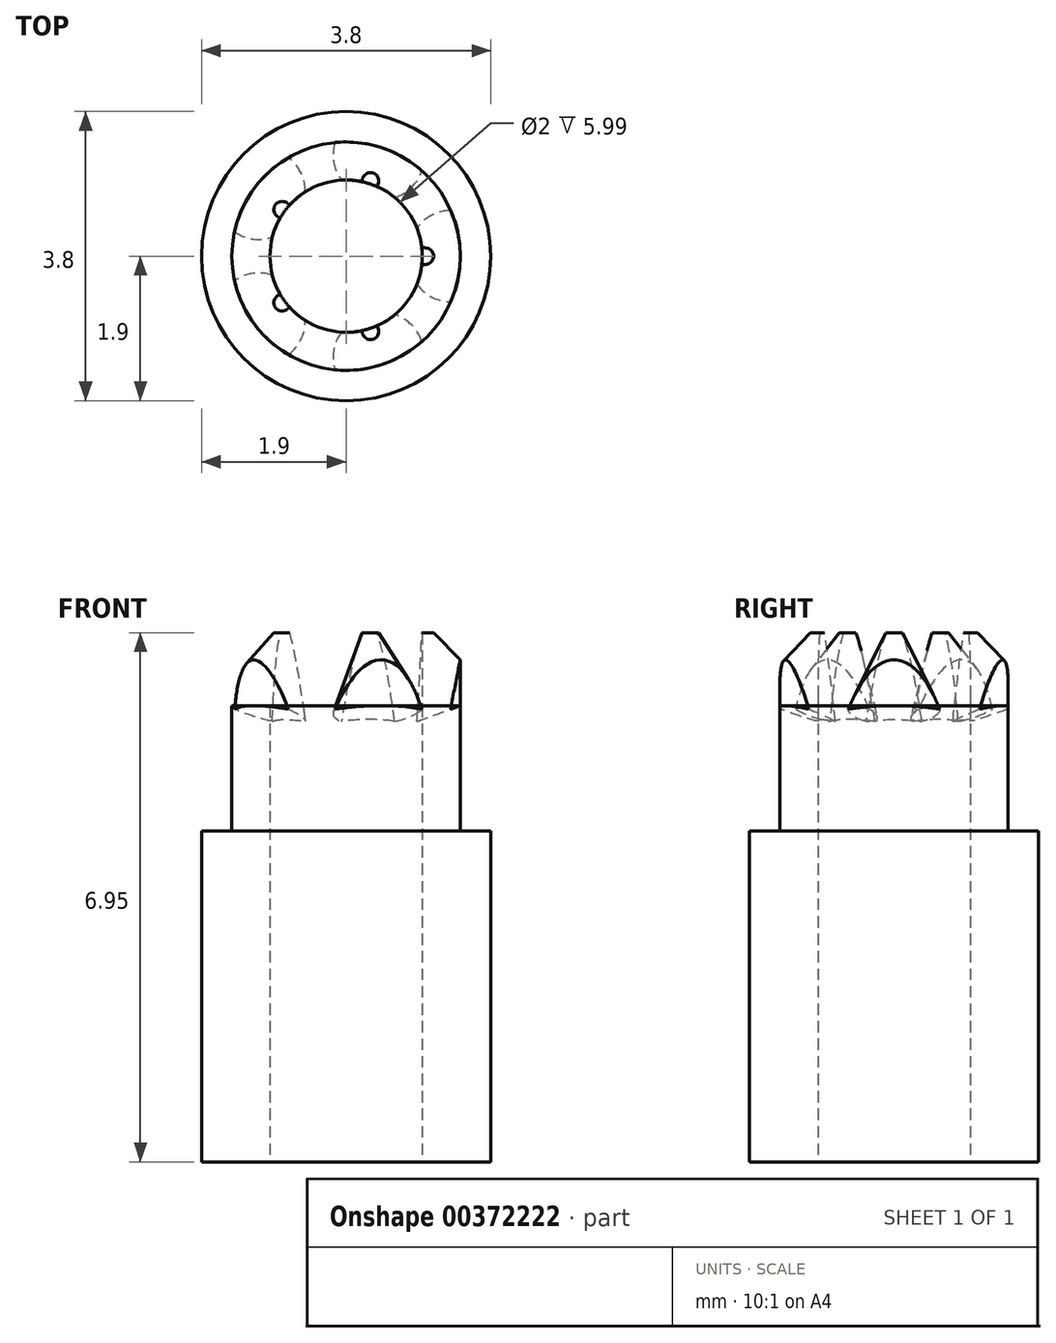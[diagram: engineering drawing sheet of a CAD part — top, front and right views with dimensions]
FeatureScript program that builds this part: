
annotation { "Feature Type Name" : "Feature", "Feature Type Description" : "" }
export const myFeature = defineFeature(function(context is Context, id is Id, definition is map)
    precondition{}
    {
        {
            var Q0;
            Q0=qCreatedBy(makeId("Top.planeOp"),FACE);
            var sketch = newSketch(context, id + "F0", { "sketchPlane" : qUnion([Q0])});
            skCircle(sketch, "E0", {"center": v(0, 0) * mm, "radius": 1 * mm});
            skCircle(sketch, "E1", {"center": v(0, 0) * mm, "radius": 1.5 * mm});
            skCircle(sketch, "E2", {"center": v(0, 0) * mm, "radius": 1.9 * mm});
            skSolve(sketch);
        }
        {
            var Q0;
            Q0=makeQuery(id+"F0.imprint","IMPRINT",FACE,{"disambiguationData":[TD([[makeQuery(id+"F0.imprint","IMPRINT",EDGE,{"derivedFrom":sQuery(id+"F0.wireOp",EDGE,"E0")}),-1.0]])]});
            extrude(context, id + "F1", {"entities" : qUnion([Q0]), "depth" : 2.6 * mm});
        }
        {
            var Q0;
            Q0=qCreatedBy(makeId("Top.planeOp"),FACE);
            cPlane(context, id + "F2", {"entities" : qUnion([Q0]), "cplaneType" : CPlaneType.OFFSET, "offset" : 1.6 * mm, "width" : 150 * mm, "height" : 150 * mm});
        }
        {
            var Q0;
            Q0=qCreatedBy(makeId("Front.planeOp"),FACE);
            var sketch = newSketch(context, id + "F3", { "sketchPlane" : qUnion([Q0])});
            skLineSegment(sketch, "E3", {"start": v(0, 0) * mm, "end": v(0, 1.6) * mm, "construction": true});
            skLineSegment(sketch, "E4", {"start": v(0, 1.6) * mm, "end": v(1.38, 1.6) * mm, "construction": true});
            skLineSegment(sketch, "E5", {"start": v(1.37, 1.6) * mm, "end": v(1.94, 1.8) * mm});
            skLineSegment(sketch, "E6", {"start": v(1.38, 1.6) * mm, "end": v(0.93, 2.82) * mm});
            skLineSegment(sketch, "E7", {"start": v(1.94, 1.8) * mm, "end": v(0.93, 2.82) * mm});
            skSolve(sketch);
        }
        {
            var Q0;
            Q0=makeQuery(id+"F3.imprint","IMPRINT",FACE,{"disambiguationData":[TD([[makeQuery(id+"F3.imprint","IMPRINT",EDGE,{"derivedFrom":sQuery(id+"F3.wireOp",EDGE,"E5")}),1.0]])]});
            var Q1;
            Q1=sQuery(id+"F3.wireOp",EDGE,"E6");
            revolve(context, id + "F4", {"entities" : qUnion([Q0]), "axis" : qUnion([Q1]), "revolveType" : RevolveType.FULL, "oppositeDirection" : true});
        }
        {
            var Q0;
            Q0=makeQuery(id+"F4.opRevolve","SWEPT_BODY",BODY,{"disambiguationData":[OSD([sQuery(id+"F3.wireOp",EDGE,"E5"),sQuery(id+"F3.wireOp",EDGE,"E6"),sQuery(id+"F3.wireOp",EDGE,"E7")])]});
            var Q1;
            Q1=sQuery(id+"F3.wireOp",EDGE,"E3");
            circularPattern(context, id + "F5", {"entities" : qUnion([Q0]), "axis" : qUnion([Q1]), "angle" : 72 * degree, "instanceCount" : round(5), "computeTransformsWithoutBuiltin" : true});
        }
        {
            var Q0;
            Q0=makeQuery(id+"F1.opExtrude","SWEPT_BODY",BODY,{"disambiguationData":[OSD([sQuery(id+"F0.wireOp",EDGE,"E0"),sQuery(id+"F0.wireOp",EDGE,"E1")])]});
            transform(context, id + "F6", {"entities" : qUnion([Q0]), "transformType" : TransformType.TRANSLATION_3D, "dx" : 0 * mm, "dy" : 0 * mm, "dz" : 0 * mm, "makeCopy" : true});
        }
        {
            var Q0;
            Q0=makeQuery(id+"F1.opExtrude","SWEPT_BODY",BODY,{"disambiguationData":[OSD([sQuery(id+"F0.wireOp",EDGE,"E0"),sQuery(id+"F0.wireOp",EDGE,"E1")])]});
            var Q1;
            Q1=makeQuery(id+"F4.opRevolve","SWEPT_BODY",BODY,{"disambiguationData":[OSD([sQuery(id+"F3.wireOp",EDGE,"E5"),sQuery(id+"F3.wireOp",EDGE,"E6"),sQuery(id+"F3.wireOp",EDGE,"E7")])]});
            booleanBodies(context, id + "F7", {"operationType" : BooleanOperationType.INTERSECTION, "tools" : qUnion([Q0, Q1])});
        }
        {
            var Q0;
            Q0=makeQuery(id+"F6.opPattern","COPY",BODY,{"derivedFrom":makeQuery(id+"F1.opExtrude","SWEPT_BODY",BODY,{"disambiguationData":[OSD([sQuery(id+"F0.wireOp",EDGE,"E0"),sQuery(id+"F0.wireOp",EDGE,"E1")])]}),"instanceName":"1"});
            transform(context, id + "F8", {"entities" : qUnion([Q0]), "transformType" : TransformType.TRANSLATION_3D, "dx" : 0 * mm, "dy" : 0 * mm, "dz" : 0 * mm, "makeCopy" : true});
        }
        {
            var Q0;
            Q0=makeQuery(id+"F8.opPattern","COPY",BODY,{"derivedFrom":makeQuery(id+"F6.opPattern","COPY",BODY,{"derivedFrom":makeQuery(id+"F1.opExtrude","SWEPT_BODY",BODY,{"disambiguationData":[OSD([sQuery(id+"F0.wireOp",EDGE,"E0"),sQuery(id+"F0.wireOp",EDGE,"E1")])]}),"instanceName":"1"}),"instanceName":"1"});
            transform(context, id + "F9", {"entities" : qUnion([Q0]), "transformType" : TransformType.TRANSLATION_3D, "dx" : 0 * mm, "dy" : 0 * mm, "dz" : 0 * mm, "makeCopy" : true});
        }
        {
            var Q0;
            Q0=makeQuery(id+"F9.opPattern","COPY",BODY,{"derivedFrom":makeQuery(id+"F8.opPattern","COPY",BODY,{"derivedFrom":makeQuery(id+"F6.opPattern","COPY",BODY,{"derivedFrom":makeQuery(id+"F1.opExtrude","SWEPT_BODY",BODY,{"disambiguationData":[OSD([sQuery(id+"F0.wireOp",EDGE,"E0"),sQuery(id+"F0.wireOp",EDGE,"E1")])]}),"instanceName":"1"}),"instanceName":"1"}),"instanceName":"1"});
            transform(context, id + "F10", {"entities" : qUnion([Q0]), "transformType" : TransformType.TRANSLATION_3D, "dx" : 0 * mm, "dy" : 0 * mm, "dz" : 0 * mm, "makeCopy" : true});
        }
        {
            var Q0;
            Q0=makeQuery(id+"F5.opPattern","COPY",BODY,{"derivedFrom":makeQuery(id+"F4.opRevolve","SWEPT_BODY",BODY,{"disambiguationData":[OSD([sQuery(id+"F3.wireOp",EDGE,"E5"),sQuery(id+"F3.wireOp",EDGE,"E6"),sQuery(id+"F3.wireOp",EDGE,"E7")])]}),"instanceName":"1"});
            var Q1;
            Q1=makeQuery(id+"F6.opPattern","COPY",BODY,{"derivedFrom":makeQuery(id+"F1.opExtrude","SWEPT_BODY",BODY,{"disambiguationData":[OSD([sQuery(id+"F0.wireOp",EDGE,"E0"),sQuery(id+"F0.wireOp",EDGE,"E1")])]}),"instanceName":"1"});
            booleanBodies(context, id + "F11", {"operationType" : BooleanOperationType.INTERSECTION, "tools" : qUnion([Q0, Q1])});
        }
        {
            var Q0;
            Q0=makeQuery(id+"F5.opPattern","COPY",BODY,{"derivedFrom":makeQuery(id+"F4.opRevolve","SWEPT_BODY",BODY,{"disambiguationData":[OSD([sQuery(id+"F3.wireOp",EDGE,"E5"),sQuery(id+"F3.wireOp",EDGE,"E6"),sQuery(id+"F3.wireOp",EDGE,"E7")])]}),"instanceName":"2"});
            var Q1;
            Q1=makeQuery(id+"F8.opPattern","COPY",BODY,{"derivedFrom":makeQuery(id+"F6.opPattern","COPY",BODY,{"derivedFrom":makeQuery(id+"F1.opExtrude","SWEPT_BODY",BODY,{"disambiguationData":[OSD([sQuery(id+"F0.wireOp",EDGE,"E0"),sQuery(id+"F0.wireOp",EDGE,"E1")])]}),"instanceName":"1"}),"instanceName":"1"});
            booleanBodies(context, id + "F12", {"operationType" : BooleanOperationType.INTERSECTION, "tools" : qUnion([Q0, Q1])});
        }
        {
            var Q0;
            Q0=makeQuery(id+"F5.opPattern","COPY",BODY,{"derivedFrom":makeQuery(id+"F4.opRevolve","SWEPT_BODY",BODY,{"disambiguationData":[OSD([sQuery(id+"F3.wireOp",EDGE,"E5"),sQuery(id+"F3.wireOp",EDGE,"E6"),sQuery(id+"F3.wireOp",EDGE,"E7")])]}),"instanceName":"3"});
            var Q1;
            Q1=makeQuery(id+"F9.opPattern","COPY",BODY,{"derivedFrom":makeQuery(id+"F8.opPattern","COPY",BODY,{"derivedFrom":makeQuery(id+"F6.opPattern","COPY",BODY,{"derivedFrom":makeQuery(id+"F1.opExtrude","SWEPT_BODY",BODY,{"disambiguationData":[OSD([sQuery(id+"F0.wireOp",EDGE,"E0"),sQuery(id+"F0.wireOp",EDGE,"E1")])]}),"instanceName":"1"}),"instanceName":"1"}),"instanceName":"1"});
            booleanBodies(context, id + "F13", {"operationType" : BooleanOperationType.INTERSECTION, "tools" : qUnion([Q0, Q1])});
        }
        {
            var Q0;
            Q0=makeQuery(id+"F10.opPattern","COPY",BODY,{"derivedFrom":makeQuery(id+"F9.opPattern","COPY",BODY,{"derivedFrom":makeQuery(id+"F8.opPattern","COPY",BODY,{"derivedFrom":makeQuery(id+"F6.opPattern","COPY",BODY,{"derivedFrom":makeQuery(id+"F1.opExtrude","SWEPT_BODY",BODY,{"disambiguationData":[OSD([sQuery(id+"F0.wireOp",EDGE,"E0"),sQuery(id+"F0.wireOp",EDGE,"E1")])]}),"instanceName":"1"}),"instanceName":"1"}),"instanceName":"1"}),"instanceName":"1"});
            transform(context, id + "F14", {"entities" : qUnion([Q0]), "transformType" : TransformType.TRANSLATION_3D, "dx" : 0 * mm, "dy" : 0 * mm, "dz" : 0 * mm, "makeCopy" : true});
        }
        {
            var Q0;
            Q0=makeQuery(id+"F10.opPattern","COPY",BODY,{"derivedFrom":makeQuery(id+"F9.opPattern","COPY",BODY,{"derivedFrom":makeQuery(id+"F8.opPattern","COPY",BODY,{"derivedFrom":makeQuery(id+"F6.opPattern","COPY",BODY,{"derivedFrom":makeQuery(id+"F1.opExtrude","SWEPT_BODY",BODY,{"disambiguationData":[OSD([sQuery(id+"F0.wireOp",EDGE,"E0"),sQuery(id+"F0.wireOp",EDGE,"E1")])]}),"instanceName":"1"}),"instanceName":"1"}),"instanceName":"1"}),"instanceName":"1"});
            var Q1;
            Q1=makeQuery(id+"F5.opPattern","COPY",BODY,{"derivedFrom":makeQuery(id+"F4.opRevolve","SWEPT_BODY",BODY,{"disambiguationData":[OSD([sQuery(id+"F3.wireOp",EDGE,"E5"),sQuery(id+"F3.wireOp",EDGE,"E6"),sQuery(id+"F3.wireOp",EDGE,"E7")])]}),"instanceName":"4"});
            booleanBodies(context, id + "F15", {"operationType" : BooleanOperationType.INTERSECTION, "tools" : qUnion([Q0, Q1])});
        }
        {
            var Q0;
            Q0=makeQuery(id+"F14.opPattern","COPY",BODY,{"derivedFrom":makeQuery(id+"F10.opPattern","COPY",BODY,{"derivedFrom":makeQuery(id+"F9.opPattern","COPY",BODY,{"derivedFrom":makeQuery(id+"F8.opPattern","COPY",BODY,{"derivedFrom":makeQuery(id+"F6.opPattern","COPY",BODY,{"derivedFrom":makeQuery(id+"F1.opExtrude","SWEPT_BODY",BODY,{"disambiguationData":[OSD([sQuery(id+"F0.wireOp",EDGE,"E0"),sQuery(id+"F0.wireOp",EDGE,"E1")])]}),"instanceName":"1"}),"instanceName":"1"}),"instanceName":"1"}),"instanceName":"1"}),"instanceName":"1"});
            deleteBodies(context, id + "F16", {"entities" : qUnion([Q0])});
        }
        {
            var Q0;
            Q0=makeQuery(id+"F0.imprint","IMPRINT",FACE,{"disambiguationData":[TD([[makeQuery(id+"F0.imprint","IMPRINT",EDGE,{"derivedFrom":sQuery(id+"F0.wireOp",EDGE,"E0")}),-1.0]])]});
            extrude(context, id + "F17", {"entities" : qUnion([Q0]), "depth" : 1.64 * mm});
        }
        {
            var Q0;
            Q0=makeQuery(id+"F0.imprint","IMPRINT",FACE,{"disambiguationData":[TD([[makeQuery(id+"F0.imprint","IMPRINT",EDGE,{"derivedFrom":sQuery(id+"F0.wireOp",EDGE,"E1")}),-1.0]])]});
            var Q1;
            Q1=makeQuery(id+"F0.imprint","IMPRINT",FACE,{"disambiguationData":[TD([[makeQuery(id+"F0.imprint","IMPRINT",EDGE,{"derivedFrom":sQuery(id+"F0.wireOp",EDGE,"E0")}),-1.0]])]});
            extrude(context, id + "F18", {"entities" : qUnion([Q0, Q1]), "operationType" : NewBodyOperationType.ADD, "oppositeDirection" : true, "depth" : 4.35 * mm});
        }
    });
